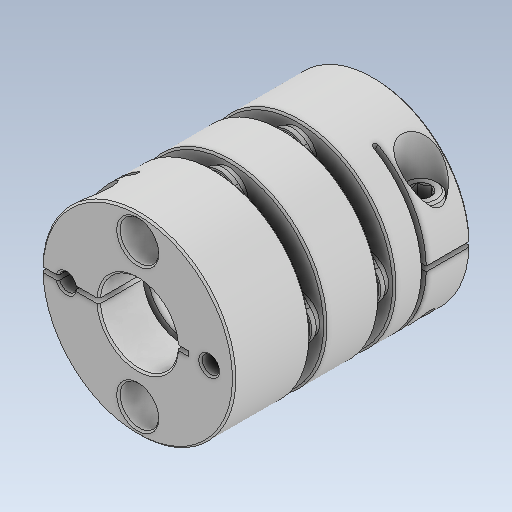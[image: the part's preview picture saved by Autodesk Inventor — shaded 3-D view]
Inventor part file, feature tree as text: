
AUTODESK INVENTOR PART (.ipt)
format: ipt  version: 2020 (Build 240168000, 168)  size: 1,468,416 bytes
history: native  units: in
note: dims shown in document units (in); Inventor stores cm internally (conversion verified against a paired STEP export)
features: chamfer x6, other x5, boolean_combine x1, pattern_circular x1
ambient origin geometry x8: Origin, YZ Plane, XZ Plane, XY Plane, X Axis, Y Axis, Z Axis, Center Point
bodies: Solid1 (feature_tree), Solid2 (feature_tree), Solid3 (feature_tree), Solid4 (feature_tree), Solid5 (feature_tree), Solid6 (feature_tree), Solid7 (feature_tree), Solid8 (feature_tree), Solid9 (feature_tree), Solid10 (feature_tree), Solid11 (feature_tree), Solid12 (feature_tree), Solid13 (feature_tree)
feature tree (13):
  boolean_combine  "Combine3"
  chamfer  "Chamfer3"  [1 undecoded]
  pattern_circular  "CirPattern2"
  chamfer  "Chamfer5"  [1 undecoded]
  other  "Boss-Extrude4"
  other  "CirPattern3[1]"
  other  "CirPattern3[2]"
  other  "CirPattern3[3]"
  other  "CirPattern3[5]"
  chamfer  "Chamfer6"  [1 undecoded]
  chamfer  "Chamfer7"  [1 undecoded]
  chamfer  "Chamfer10"  [1 undecoded]
  chamfer  "Chamfer11"  [1 undecoded]
note: 6 required parameter values undecoded (feature->parameter linkage not recoverable at this tier; creation-order binding heuristic only, values carry confidence <= 0.55)
